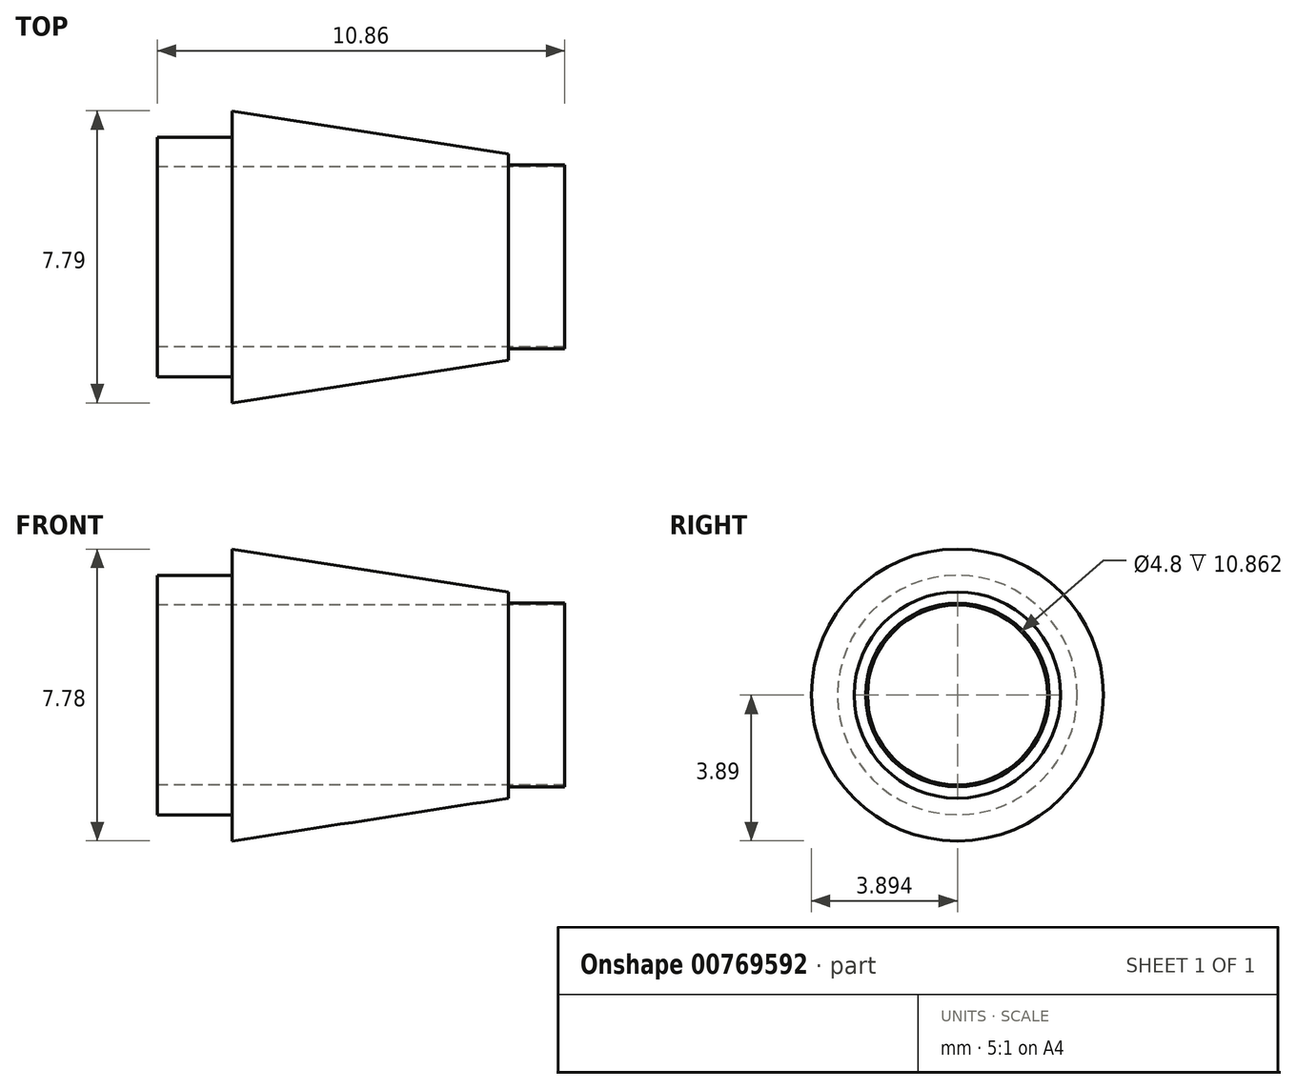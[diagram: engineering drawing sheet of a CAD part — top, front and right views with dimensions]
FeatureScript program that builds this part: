
annotation { "Feature Type Name" : "Feature", "Feature Type Description" : "" }
export const myFeature = defineFeature(function(context is Context, id is Id, definition is map)
    precondition{}
    {
        {
            var Q0;
            Q0=qCreatedBy(makeId("Top.planeOp"),FACE);
            var sketch = newSketch(context, id + "F0", { "sketchPlane" : qUnion([Q0])});
            skLineSegment(sketch, "E0", {"start": v(-31.94, 22.02) * mm, "end": v(-29.94, 22.02) * mm});
            skLineSegment(sketch, "E1", {"start": v(-29.94, 22.02) * mm, "end": v(-29.94, 22.72) * mm});
            skLineSegment(sketch, "E2", {"start": v(-29.94, 22.72) * mm, "end": v(-22.58, 21.57) * mm});
            skLineSegment(sketch, "E3", {"start": v(-22.58, 21.57) * mm, "end": v(-22.58, 21.27) * mm});
            skLineSegment(sketch, "E4", {"start": v(-22.58, 21.27) * mm, "end": v(-21.08, 21.27) * mm});
            skLineSegment(sketch, "E5", {"start": v(-21.08, 21.27) * mm, "end": v(-21.08, 18.82) * mm});
            skLineSegment(sketch, "E6", {"start": v(-31.94, 19.82) * mm, "end": v(-31.94, 22.02) * mm});
            skPoint(sketch, "E7.orphan", {"position": v(-21.08, 16.37) * mm});
            skLineSegment(sketch, "E8", {"start": v(-21.08, 18.82) * mm, "end": v(-21.08, 16.37) * mm});
            skLineSegment(sketch, "E9", {"start": v(-21.08, 18.82) * mm, "end": v(-31.94, 18.82) * mm});
            skLineSegment(sketch, "E10", {"start": v(-31.94, 18.82) * mm, "end": v(-31.94, 19.82) * mm});
            skSolve(sketch);
        }
        {
            var Q0;
            Q0=makeQuery(id+"F0.imprint","IMPRINT",FACE,{"disambiguationData":[TD([[makeQuery(id+"F0.imprint","IMPRINT",EDGE,{"derivedFrom":sQuery(id+"F0.wireOp",EDGE,"E0")}),-1.0]])]});
            var Q1;
            Q1=sQuery(id+"F0.wireOp",EDGE,"E9");
            revolve(context, id + "F1", {"surfaceOperationType" : NewSurfaceOperationType.NEW, "entities" : qUnion([Q0]), "axis" : qUnion([Q1]), "revolveType" : RevolveType.FULL});
        }
        {
            var Q0;
            Q0=makeQuery(id+"F1.opRevolve","SWEPT_FACE",FACE,{"disambiguationData":[OSD([sQuery(id+"F0.wireOp",EDGE,"E6"),sQuery(id+"F0.wireOp",EDGE,"E10")])]});
            var sketch = newSketch(context, id + "F2", { "sketchPlane" : qUnion([Q0])});
            skCircle(sketch, "E11", {"center": v(-18.82, 0) * mm, "radius": 2.4 * mm});
            skSolve(sketch);
        }
        {
            var Q0;
            Q0 = qSketchRegion(id + "F2", true);
            extrude(context, id + "F3", {"entities" : qUnion([Q0]), "operationType" : NewBodyOperationType.REMOVE, "oppositeDirection" : true, "depth" : 25 * mm, "offsetDistance" : 25 * mm});
        }
    });
